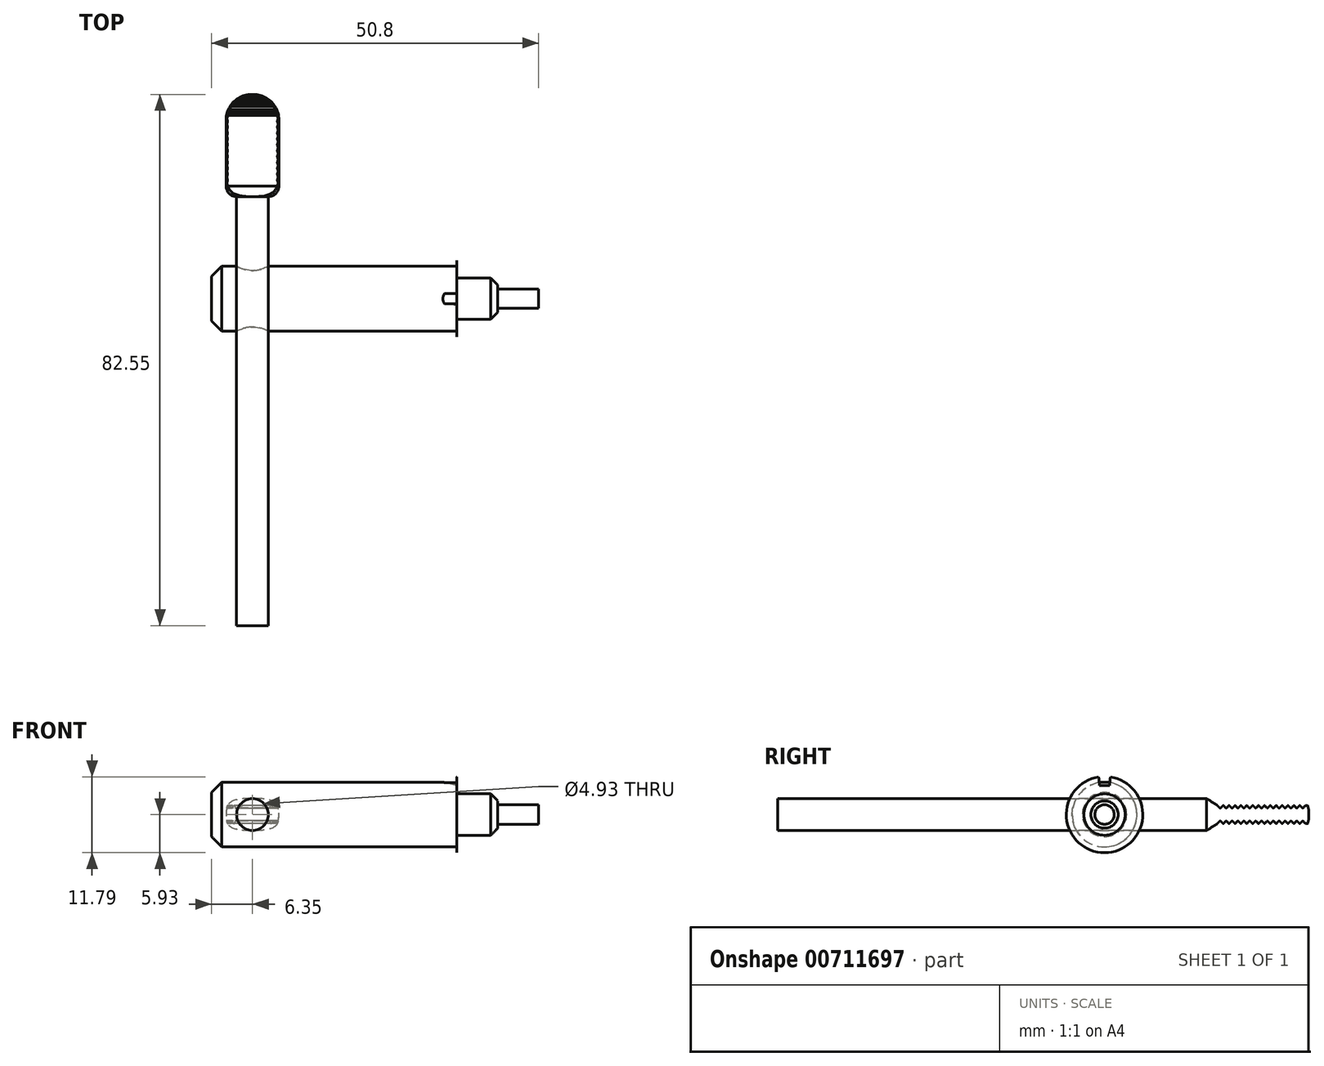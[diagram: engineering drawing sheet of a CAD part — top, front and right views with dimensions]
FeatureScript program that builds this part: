
annotation { "Feature Type Name" : "Feature", "Feature Type Description" : "" }
export const myFeature = defineFeature(function(context is Context, id is Id, definition is map)
    precondition{}
    {
        {
            var Q0;
            Q0=qCreatedBy(makeId("Right.planeOp"),FACE);
            var sketch = newSketch(context, id + "F0", { "sketchPlane" : qUnion([Q0])});
            skCircle(sketch, "E0", {"center": v(0, 0) * mm, "radius": 5.03 * mm});
            skSolve(sketch);
        }
        {
            var Q0;
            Q0 = qSketchRegion(id + "F0", true);
            extrude(context, id + "F1", {"entities" : qUnion([Q0]), "depth" : 38.1 * mm, "offsetDistance" : 25.4 * mm});
        }
        {
            var Q0;
            Q0=makeQuery(id+"F1.opExtrude","CAP_FACE",FACE,{"disambiguationData":[OSD([sQuery(id+"F0.wireOp",EDGE,"E0")])],"isStart":false});
            var sketch = newSketch(context, id + "F2", { "sketchPlane" : qUnion([Q0])});
            skCircle(sketch, "E1", {"center": v(0, 0) * mm, "radius": 7.14 * mm});
            skSolve(sketch);
        }
        {
            var Q0;
            Q0 = qSketchRegion(id + "F2", true);
            extrude(context, id + "F3", {"entities" : qUnion([Q0]), "operationType" : NewBodyOperationType.ADD, "oppositeDirection" : true, "depth" : 5 / 406.4 * mm, "offsetDistance" : 25.4 * mm, "hasDraft" : true, "draftAngle" : 22 * degree});
        }
        {
            var Q0;
            Q0=makeQuery(id+"F3.boolean.opBoolean","MERGE",FACE,{"derivedFrom":[makeQuery(id+"F1.opExtrude","CAP_FACE",FACE,{"disambiguationData":[OSD([sQuery(id+"F0.wireOp",EDGE,"E0")])],"isStart":false}),makeQuery(id+"F3.opExtrude","CAP_FACE",FACE,{"disambiguationData":[OSD([sQuery(id+"F2.wireOp",EDGE,"E1")])],"isStart":true})]});
            var sketch = newSketch(context, id + "F4", { "sketchPlane" : qUnion([Q0])});
            skCircle(sketch, "E2", {"center": v(0, 0) * mm, "radius": 3.22 * mm});
            skSolve(sketch);
        }
        {
            var Q0;
            Q0 = qSketchRegion(id + "F4", true);
            extrude(context, id + "F5", {"entities" : qUnion([Q0]), "operationType" : NewBodyOperationType.ADD, "depth" : 6.35 * mm, "offsetDistance" : 25.4 * mm});
        }
        {
            var Q0;
            Q0=makeQuery(id+"F5.opExtrude","CAP_FACE",FACE,{"disambiguationData":[OSD([sQuery(id+"F4.wireOp",EDGE,"E2")])],"isStart":false});
            var sketch = newSketch(context, id + "F6", { "sketchPlane" : qUnion([Q0])});
            skCircle(sketch, "E3", {"center": v(0, 0) * mm, "radius": 1.51 * mm});
            skSolve(sketch);
        }
        {
            var Q0;
            Q0 = qSketchRegion(id + "F6", true);
            extrude(context, id + "F7", {"entities" : qUnion([Q0]), "operationType" : NewBodyOperationType.ADD, "depth" : 6.35 * mm, "offsetDistance" : 25.4 * mm});
        }
        {
            var Q0;
            Q0=makeQuery(id+"F5.opExtrude","CAP_EDGE",EDGE,{"disambiguationData":[OSD([sQuery(id+"F4.wireOp",EDGE,"E2")])],"isStart":false});
            chamfer(context, id + "F8", {"entities" : qUnion([Q0]), "chamferType" : ChamferType.OFFSET_ANGLE, "width" : 1.1 * mm, "oppositeDirection" : false, "angle" : 45 * degree, "tangentPropagation" : true});
        }
        {
            var Q0;
            Q0=makeQuery(id+"F1.opExtrude","CAP_EDGE",EDGE,{"disambiguationData":[OSD([sQuery(id+"F0.wireOp",EDGE,"E0")])],"isStart":true});
            chamfer(context, id + "F9", {"entities" : qUnion([Q0]), "chamferType" : ChamferType.OFFSET_ANGLE, "width" : 1.59 * mm, "oppositeDirection" : false, "angle" : 45 * degree, "tangentPropagation" : true});
        }
        {
            var Q0;
            Q0=makeQuery(id+"F3.opExtrude","CAP_EDGE",EDGE,{"disambiguationData":[OSD([sQuery(id+"F2.wireOp",EDGE,"E1")])],"isStart":false});
            chamfer(context, id + "F10", {"entities" : qUnion([Q0]), "chamferType" : ChamferType.OFFSET_ANGLE, "width" : 1.59 * mm, "oppositeDirection" : false, "angle" : 45 * degree, "tangentPropagation" : true});
        }
        {
            var Q0;
            Q0=qCreatedBy(makeId("Front.planeOp"),FACE);
            var sketch = newSketch(context, id + "F11", { "sketchPlane" : qUnion([Q0])});
            skLineSegment(sketch, "E4", {"start": v(57.18, 0) * mm, "end": v(30.16, 6.4) * mm});
            skLineSegment(sketch, "E5", {"start": v(30.16, 0) * mm, "end": v(0, 0) * mm});
            skLineSegment(sketch, "E6", {"start": v(30.16, 6.4) * mm, "end": v(30.16, 11.7) * mm});
            skLineSegment(sketch, "E7", {"start": v(30.16, 11.7) * mm, "end": v(57.18, 0) * mm});
            skSolve(sketch);
        }
        {
            var Q0;
            Q0 = qSketchRegion(id + "F11", true);
            extrude(context, id + "F12", {"entities" : qUnion([Q0]), "operationType" : NewBodyOperationType.REMOVE, "depth" : 0.8 * mm, "offsetDistance" : 25.4 * mm, "hasSecondDirection" : true, "secondDirectionOppositeDirection" : true, "secondDirectionDepth" : 0.8 * mm});
        }
        {
            var Q0;
            {var subQ3=sQuery(id+"F11.wireOp",EDGE,"E4");Q0=makeQuery(id+"F12.boolean.opBoolean","COPY",FACE,{"disambiguationData":[TD([makeQuery(id+"F1.opExtrude","CAP_FACE",FACE,{"disambiguationData":[OSD([sQuery(id+"F0.wireOp",EDGE,"E0")])],"isStart":false})])],"derivedFrom":makeQuery(id+"F12.opExtrude","SWEPT_FACE",FACE,{"disambiguationData":[OSD([subQ3])]})});}
            var sketch = newSketch(context, id + "F13", { "sketchPlane" : qUnion([Q0])});
            skLineSegment(sketch, "E8.bottom", {"start": v(34.32, -0.8) * mm, "end": v(31.78, -0.8) * mm});
            skLineSegment(sketch, "E8.top", {"start": v(34.32, 0.8) * mm, "end": v(31.78, 0.8) * mm});
            skLineSegment(sketch, "E8.left", {"start": v(34.32, -0.8) * mm, "end": v(34.32, 0.8) * mm});
            skLineSegment(sketch, "E8.right", {"start": v(31.78, -0.8) * mm, "end": v(31.78, 0.8) * mm});
            skSolve(sketch);
        }
        {
            var Q0;
            Q0 = qSketchRegion(id + "F13", true);
            extrude(context, id + "F14", {"entities" : qUnion([Q0]), "operationType" : NewBodyOperationType.ADD, "depth" : 12.7 * mm, "offsetDistance" : 25.4 * mm});
        }
        {
            var Q0;
            Q0=makeQuery(id+"F14.opExtrude","SWEPT_FACE",FACE,{"disambiguationData":[OSD([sQuery(id+"F13.wireOp",EDGE,"E8.left")])]});
            var sketch = newSketch(context, id + "F15", { "sketchPlane" : qUnion([Q0])});
            skFitSpline(sketch, "E9", {"points": [v(0.8, 13.16) * mm, v(0.85, 13.93) * mm, v(1.13, 15.04) * mm, v(2.24, 16.6) * mm], "startDerivative": vector(0.1, 2.28) * mm, "endDerivative": vector(1.27, 1.84) * mm});
            skLineSegment(sketch, "E10", {"start": v(-0.8, 13.16) * mm, "end": v(0.8, 13.16) * mm});
            skFitSpline(sketch, "E11.MirrorCS", {"points": [v(-0.8, 13.16) * mm, v(-0.85, 13.93) * mm, v(-1.13, 15.04) * mm, v(-2.24, 16.6) * mm], "startDerivative": vector(-0.1, 2.28) * mm, "endDerivative": vector(-1.27, 1.84) * mm});
            skArc(sketch, "E12", {"start": v(2.24, 16.6) * mm, "mid": v(0, 17.44) * mm, "end": v(-2.24, 16.6) * mm});
            skSolve(sketch);
        }
        {
            var Q0;
            Q0 = qSketchRegion(id + "F15", true);
            extrude(context, id + "F16", {"entities" : qUnion([Q0]), "operationType" : NewBodyOperationType.REMOVE, "depth" : 25.4 * mm, "offsetDistance" : 25.4 * mm, "hasSecondDirection" : true, "secondDirectionOppositeDirection" : true, "secondDirectionDepth" : 25.4 * mm});
        }
        {
            var Q0;
            Q0=makeQuery(id+"F14.opExtrude","SWEPT_FACE",FACE,{"disambiguationData":[OSD([sQuery(id+"F13.wireOp",EDGE,"E8.left")])]});
            var sketch = newSketch(context, id + "F17", { "sketchPlane" : qUnion([Q0])});
            skLineSegment(sketch, "E13.bottom", {"start": v(-0.8, 25.86) * mm, "end": v(0.8, 25.86) * mm});
            skLineSegment(sketch, "E13.top", {"start": v(-0.8, 17.34) * mm, "end": v(0.8, 17.34) * mm});
            skLineSegment(sketch, "E13.left", {"start": v(-0.8, 25.86) * mm, "end": v(-0.8, 17.34) * mm});
            skLineSegment(sketch, "E13.right", {"start": v(0.8, 25.86) * mm, "end": v(0.8, 17.34) * mm});
            skSolve(sketch);
        }
        {
            var Q0;
            Q0 = qSketchRegion(id + "F17", true);
            extrude(context, id + "F18", {"entities" : qUnion([Q0]), "operationType" : NewBodyOperationType.REMOVE, "oppositeDirection" : true, "depth" : 25.4 * mm, "offsetDistance" : 25.4 * mm});
        }
        {
            var Q0;
            Q0=qCreatedBy(makeId("Front.planeOp"),FACE);
            var sketch = newSketch(context, id + "F19", { "sketchPlane" : qUnion([Q0])});
            skCircle(sketch, "E14", {"center": v(6.35, 0) * mm, "radius": 2.46 * mm});
            skSolve(sketch);
        }
        {
            var Q0;
            Q0 = qSketchRegion(id + "F19", true);
            extrude(context, id + "F20", {"entities" : qUnion([Q0]), "operationType" : NewBodyOperationType.REMOVE, "oppositeDirection" : true, "depth" : 25.4 * mm, "offsetDistance" : 25.4 * mm, "hasSecondDirection" : true, "secondDirectionOppositeDirection" : false, "secondDirectionDepth" : 25.4 * mm});
        }
        {
            var Q0;
            Q0=qCreatedBy(makeId("Front.planeOp"),FACE);
            var sketch = newSketch(context, id + "F21", { "sketchPlane" : qUnion([Q0])});
            skCircle(sketch, "E15", {"center": v(6.35, 0) * mm, "radius": 2.46 * mm});
            skSolve(sketch);
        }
        {
            var Q0;
            Q0 = qSketchRegion(id + "F21", true);
            extrude(context, id + "F22", {"entities" : qUnion([Q0]), "depth" : 50.8 * mm, "offsetDistance" : 25.4 * mm, "hasSecondDirection" : true, "secondDirectionOppositeDirection" : true, "secondDirectionDepth" : 31.75 * mm});
        }
        {
            var Q0;
            Q0=makeQuery(id+"F22.opExtrude","CAP_FACE",FACE,{"disambiguationData":[OSD([sQuery(id+"F21.wireOp",EDGE,"E15")])],"isStart":true});
            var sketch = newSketch(context, id + "F23", { "sketchPlane" : qUnion([Q0])});
            skCircle(sketch, "E16", {"center": v(-6.35, 0) * mm, "radius": 4.1 * mm});
            skSolve(sketch);
        }
        {
            var Q0;
            Q0 = qSketchRegion(id + "F23", true);
            extrude(context, id + "F24", {"entities" : qUnion([Q0]), "operationType" : NewBodyOperationType.ADD, "oppositeDirection" : true, "depth" : 15.88 * mm, "offsetDistance" : 25.4 * mm});
        }
        {
            var Q0;
            Q0=qCreatedBy(makeId("Right.planeOp"),FACE);
            var sketch = newSketch(context, id + "F25", { "sketchPlane" : qUnion([Q0])});
            skLineSegment(sketch, "E17.bottom", {"start": v(31.75, 1.42) * mm, "end": v(31.24, 1.42) * mm});
            skLineSegment(sketch, "E17.top", {"start": v(31.75, 6.1) * mm, "end": v(15.88, 6.1) * mm});
            skLineSegment(sketch, "E17.left", {"start": v(31.75, 1.42) * mm, "end": v(31.75, 6.1) * mm});
            skLineSegment(sketch, "E17.right", {"start": v(15.88, 2.48) * mm, "end": v(15.88, 6.1) * mm});
            skLineSegment(sketch, "E18", {"start": v(15.88, 2.48) * mm, "end": v(17.52, 1.42) * mm});
            skLineSegment(sketch, "E19", {"start": v(17.52, 1.42) * mm, "end": v(17.89, 1.06) * mm});
            skLineSegment(sketch, "E20", {"start": v(18.07, 1.06) * mm, "end": v(18.38, 1.37) * mm});
            skLineSegment(sketch, "E21.1.0.0", {"start": v(18.49, 1.37) * mm, "end": v(18.84, 1.02) * mm});
            skLineSegment(sketch, "E21.1.0.1", {"start": v(18.95, 1.02) * mm, "end": v(19.3, 1.37) * mm});
            skLineSegment(sketch, "E21.2.0.0", {"start": v(19.4, 1.37) * mm, "end": v(19.75, 1.02) * mm});
            skLineSegment(sketch, "E21.2.0.1", {"start": v(19.86, 1.02) * mm, "end": v(20.21, 1.37) * mm});
            skLineSegment(sketch, "E21.3.0.0", {"start": v(20.32, 1.37) * mm, "end": v(20.67, 1.02) * mm});
            skLineSegment(sketch, "E21.3.0.1", {"start": v(20.78, 1.02) * mm, "end": v(21.13, 1.37) * mm});
            skLineSegment(sketch, "E21.4.0.0", {"start": v(21.23, 1.37) * mm, "end": v(21.58, 1.02) * mm});
            skLineSegment(sketch, "E21.4.0.1", {"start": v(21.7, 1.02) * mm, "end": v(22.04, 1.37) * mm});
            skLineSegment(sketch, "E21.5.0.0", {"start": v(22.15, 1.37) * mm, "end": v(22.5, 1.02) * mm});
            skLineSegment(sketch, "E21.5.0.1", {"start": v(22.6, 1.02) * mm, "end": v(22.95, 1.37) * mm});
            skLineSegment(sketch, "E21.6.0.0", {"start": v(23.06, 1.37) * mm, "end": v(23.41, 1.02) * mm});
            skLineSegment(sketch, "E21.6.0.1", {"start": v(23.52, 1.02) * mm, "end": v(23.87, 1.37) * mm});
            skLineSegment(sketch, "E21.7.0.0", {"start": v(23.98, 1.37) * mm, "end": v(24.33, 1.02) * mm});
            skLineSegment(sketch, "E21.7.0.1", {"start": v(24.43, 1.02) * mm, "end": v(24.78, 1.37) * mm});
            skLineSegment(sketch, "E21.8.0.0", {"start": v(24.9, 1.37) * mm, "end": v(25.24, 1.02) * mm});
            skLineSegment(sketch, "E21.8.0.1", {"start": v(25.35, 1.02) * mm, "end": v(25.7, 1.37) * mm});
            skLineSegment(sketch, "E21.9.0.0", {"start": v(25.8, 1.37) * mm, "end": v(26.15, 1.02) * mm});
            skLineSegment(sketch, "E21.9.0.1", {"start": v(26.26, 1.02) * mm, "end": v(26.61, 1.37) * mm});
            skLineSegment(sketch, "E21.10.0.0", {"start": v(26.72, 1.37) * mm, "end": v(27.07, 1.02) * mm});
            skLineSegment(sketch, "E21.10.0.1", {"start": v(27.18, 1.02) * mm, "end": v(27.53, 1.37) * mm});
            skLineSegment(sketch, "E21.11.0.0", {"start": v(27.63, 1.37) * mm, "end": v(27.98, 1.02) * mm});
            skLineSegment(sketch, "E21.11.0.1", {"start": v(28.1, 1.02) * mm, "end": v(28.5, 1.42) * mm});
            skLineSegment(sketch, "E21.12.0.0", {"start": v(28.5, 1.42) * mm, "end": v(28.95, 0.97) * mm});
            skLineSegment(sketch, "E21.12.0.1", {"start": v(28.95, 0.97) * mm, "end": v(29.4, 1.42) * mm});
            skLineSegment(sketch, "E21.13.0.0", {"start": v(29.4, 1.42) * mm, "end": v(29.87, 0.97) * mm});
            skLineSegment(sketch, "E21.13.0.1", {"start": v(29.87, 0.97) * mm, "end": v(30.32, 1.42) * mm});
            skLineSegment(sketch, "E21.direction1", {"start": v(17.98, 0.97) * mm, "end": v(18.9, 0.97) * mm, "construction": true});
            skLineSegment(sketch, "E22.0.14.0", {"start": v(30.32, 1.42) * mm, "end": v(30.78, 0.97) * mm});
            skLineSegment(sketch, "E22.3.14.0", {"start": v(30.78, 0.97) * mm, "end": v(31.24, 1.42) * mm});
            skPoint(sketch, "E23.visualSharp", {"position": v(17.98, 0.97) * mm});
            skArc(sketch, "E23.filletArc", {"start": v(17.89, 1.06) * mm, "mid": v(17.98, 1.02) * mm, "end": v(18.07, 1.06) * mm});
            skPoint(sketch, "E24.visualSharp", {"position": v(18.44, 1.42) * mm});
            skArc(sketch, "E24.filletArc", {"start": v(18.49, 1.37) * mm, "mid": v(18.44, 1.4) * mm, "end": v(18.38, 1.37) * mm});
            skPoint(sketch, "E25.visualSharp", {"position": v(18.9, 0.97) * mm});
            skArc(sketch, "E25.filletArc", {"start": v(18.84, 1.02) * mm, "mid": v(18.9, 1) * mm, "end": v(18.95, 1.02) * mm});
            skPoint(sketch, "E26.visualSharp", {"position": v(19.35, 1.42) * mm});
            skArc(sketch, "E26.filletArc", {"start": v(19.4, 1.37) * mm, "mid": v(19.35, 1.4) * mm, "end": v(19.3, 1.37) * mm});
            skPoint(sketch, "E27.visualSharp", {"position": v(19.8, 0.97) * mm});
            skArc(sketch, "E27.filletArc", {"start": v(19.75, 1.02) * mm, "mid": v(19.8, 1) * mm, "end": v(19.86, 1.02) * mm});
            skPoint(sketch, "E28.visualSharp", {"position": v(20.26, 1.42) * mm});
            skArc(sketch, "E28.filletArc", {"start": v(20.32, 1.37) * mm, "mid": v(20.26, 1.4) * mm, "end": v(20.21, 1.37) * mm});
            skPoint(sketch, "E29.visualSharp", {"position": v(20.72, 0.97) * mm});
            skArc(sketch, "E29.filletArc", {"start": v(20.67, 1.02) * mm, "mid": v(20.72, 1) * mm, "end": v(20.78, 1.02) * mm});
            skPoint(sketch, "E30.visualSharp", {"position": v(21.18, 1.42) * mm});
            skArc(sketch, "E30.filletArc", {"start": v(21.23, 1.37) * mm, "mid": v(21.18, 1.4) * mm, "end": v(21.13, 1.37) * mm});
            skPoint(sketch, "E31.visualSharp", {"position": v(21.64, 0.97) * mm});
            skArc(sketch, "E31.filletArc", {"start": v(21.58, 1.02) * mm, "mid": v(21.64, 1) * mm, "end": v(21.7, 1.02) * mm});
            skPoint(sketch, "E32.visualSharp", {"position": v(22.1, 1.42) * mm});
            skArc(sketch, "E32.filletArc", {"start": v(22.15, 1.37) * mm, "mid": v(22.1, 1.4) * mm, "end": v(22.04, 1.37) * mm});
            skPoint(sketch, "E33.visualSharp", {"position": v(22.55, 0.97) * mm});
            skArc(sketch, "E33.filletArc", {"start": v(22.5, 1.02) * mm, "mid": v(22.55, 1) * mm, "end": v(22.6, 1.02) * mm});
            skPoint(sketch, "E34.visualSharp", {"position": v(23, 1.42) * mm});
            skArc(sketch, "E34.filletArc", {"start": v(23.06, 1.37) * mm, "mid": v(23, 1.4) * mm, "end": v(22.95, 1.37) * mm});
            skPoint(sketch, "E35.visualSharp", {"position": v(23.92, 1.42) * mm});
            skArc(sketch, "E35.filletArc", {"start": v(23.98, 1.37) * mm, "mid": v(23.92, 1.4) * mm, "end": v(23.87, 1.37) * mm});
            skPoint(sketch, "E36.visualSharp", {"position": v(23.47, 0.97) * mm});
            skArc(sketch, "E36.filletArc", {"start": v(23.41, 1.02) * mm, "mid": v(23.47, 1) * mm, "end": v(23.52, 1.02) * mm});
            skPoint(sketch, "E37.visualSharp", {"position": v(24.38, 0.97) * mm});
            skArc(sketch, "E37.filletArc", {"start": v(24.33, 1.02) * mm, "mid": v(24.38, 1) * mm, "end": v(24.43, 1.02) * mm});
            skPoint(sketch, "E38.visualSharp", {"position": v(24.84, 1.42) * mm});
            skArc(sketch, "E38.filletArc", {"start": v(24.9, 1.37) * mm, "mid": v(24.84, 1.4) * mm, "end": v(24.78, 1.37) * mm});
            skPoint(sketch, "E39.visualSharp", {"position": v(25.75, 1.42) * mm});
            skArc(sketch, "E39.filletArc", {"start": v(25.8, 1.37) * mm, "mid": v(25.75, 1.4) * mm, "end": v(25.7, 1.37) * mm});
            skPoint(sketch, "E40.visualSharp", {"position": v(25.3, 0.97) * mm});
            skArc(sketch, "E40.filletArc", {"start": v(25.24, 1.02) * mm, "mid": v(25.3, 1) * mm, "end": v(25.35, 1.02) * mm});
            skPoint(sketch, "E41.visualSharp", {"position": v(26.2, 0.97) * mm});
            skArc(sketch, "E41.filletArc", {"start": v(26.15, 1.02) * mm, "mid": v(26.2, 1) * mm, "end": v(26.26, 1.02) * mm});
            skPoint(sketch, "E42.visualSharp", {"position": v(26.67, 1.42) * mm});
            skArc(sketch, "E42.filletArc", {"start": v(26.72, 1.37) * mm, "mid": v(26.67, 1.4) * mm, "end": v(26.61, 1.37) * mm});
            skPoint(sketch, "E43.visualSharp", {"position": v(27.58, 1.42) * mm});
            skArc(sketch, "E43.filletArc", {"start": v(27.63, 1.37) * mm, "mid": v(27.58, 1.4) * mm, "end": v(27.53, 1.37) * mm});
            skPoint(sketch, "E44.visualSharp", {"position": v(27.12, 0.97) * mm});
            skArc(sketch, "E44.filletArc", {"start": v(27.07, 1.02) * mm, "mid": v(27.12, 1) * mm, "end": v(27.18, 1.02) * mm});
            skPoint(sketch, "E45.visualSharp", {"position": v(28.04, 0.97) * mm});
            skArc(sketch, "E45.filletArc", {"start": v(27.98, 1.02) * mm, "mid": v(28.04, 1) * mm, "end": v(28.1, 1.02) * mm});
            skLineSegment(sketch, "E46.MirrorCS", {"start": v(19.4, -1.37) * mm, "end": v(19.75, -1.02) * mm});
            skArc(sketch, "E47.MirrorCS", {"start": v(22.15, -1.37) * mm, "mid": v(22.1, -1.4) * mm, "end": v(22.04, -1.37) * mm});
            skLineSegment(sketch, "E48.MirrorCS", {"start": v(18.95, -1.02) * mm, "end": v(19.3, -1.37) * mm});
            skLineSegment(sketch, "E49.MirrorCS", {"start": v(20.32, -1.37) * mm, "end": v(20.67, -1.02) * mm});
            skLineSegment(sketch, "E50.MirrorCS", {"start": v(19.86, -1.02) * mm, "end": v(20.21, -1.37) * mm});
            skLineSegment(sketch, "E51.MirrorCS", {"start": v(22.15, -1.37) * mm, "end": v(22.5, -1.02) * mm});
            skLineSegment(sketch, "E52.MirrorCS", {"start": v(21.7, -1.02) * mm, "end": v(22.04, -1.37) * mm});
            skLineSegment(sketch, "E53.MirrorCS", {"start": v(22.6, -1.02) * mm, "end": v(22.95, -1.37) * mm});
            skArc(sketch, "E54.MirrorCS", {"start": v(25.8, -1.37) * mm, "mid": v(25.75, -1.4) * mm, "end": v(25.7, -1.37) * mm});
            skLineSegment(sketch, "E55.MirrorCS", {"start": v(20.78, -1.02) * mm, "end": v(21.13, -1.37) * mm});
            skArc(sketch, "E56.MirrorCS", {"start": v(27.98, -1.02) * mm, "mid": v(28.04, -1) * mm, "end": v(28.1, -1.02) * mm});
            skLineSegment(sketch, "E57.MirrorCS", {"start": v(21.23, -1.37) * mm, "end": v(21.58, -1.02) * mm});
            skArc(sketch, "E58.MirrorCS", {"start": v(19.4, -1.37) * mm, "mid": v(19.35, -1.4) * mm, "end": v(19.3, -1.37) * mm});
            skArc(sketch, "E59.MirrorCS", {"start": v(20.67, -1.02) * mm, "mid": v(20.72, -1) * mm, "end": v(20.78, -1.02) * mm});
            skLineSegment(sketch, "E60.MirrorCS", {"start": v(27.18, -1.02) * mm, "end": v(27.53, -1.37) * mm});
            skArc(sketch, "E61.MirrorCS", {"start": v(23.06, -1.37) * mm, "mid": v(23, -1.4) * mm, "end": v(22.95, -1.37) * mm});
            skArc(sketch, "E62.MirrorCS", {"start": v(21.58, -1.02) * mm, "mid": v(21.64, -1) * mm, "end": v(21.7, -1.02) * mm});
            skLineSegment(sketch, "E63.MirrorCS", {"start": v(25.35, -1.02) * mm, "end": v(25.7, -1.37) * mm});
            skArc(sketch, "E64.MirrorCS", {"start": v(22.5, -1.02) * mm, "mid": v(22.55, -1) * mm, "end": v(22.6, -1.02) * mm});
            skLineSegment(sketch, "E65.MirrorCS", {"start": v(26.26, -1.02) * mm, "end": v(26.61, -1.37) * mm});
            skArc(sketch, "E66.MirrorCS", {"start": v(19.75, -1.02) * mm, "mid": v(19.8, -1) * mm, "end": v(19.86, -1.02) * mm});
            skArc(sketch, "E67.MirrorCS", {"start": v(18.84, -1.02) * mm, "mid": v(18.9, -1) * mm, "end": v(18.95, -1.02) * mm});
            skArc(sketch, "E68.MirrorCS", {"start": v(20.32, -1.37) * mm, "mid": v(20.26, -1.4) * mm, "end": v(20.21, -1.37) * mm});
            skArc(sketch, "E69.MirrorCS", {"start": v(21.23, -1.37) * mm, "mid": v(21.18, -1.4) * mm, "end": v(21.13, -1.37) * mm});
            skArc(sketch, "E70.MirrorCS", {"start": v(26.72, -1.37) * mm, "mid": v(26.67, -1.4) * mm, "end": v(26.61, -1.37) * mm});
            skLineSegment(sketch, "E71.MirrorCS", {"start": v(25.8, -1.37) * mm, "end": v(26.15, -1.02) * mm});
            skLineSegment(sketch, "E72.MirrorCS", {"start": v(28.1, -1.02) * mm, "end": v(28.5, -1.42) * mm});
            skLineSegment(sketch, "E73.MirrorCS", {"start": v(28.5, -1.42) * mm, "end": v(28.95, -0.97) * mm});
            skLineSegment(sketch, "E74.MirrorCS", {"start": v(26.72, -1.37) * mm, "end": v(27.07, -1.02) * mm});
            skArc(sketch, "E75.MirrorCS", {"start": v(27.63, -1.37) * mm, "mid": v(27.58, -1.4) * mm, "end": v(27.53, -1.37) * mm});
            skLineSegment(sketch, "E76.MirrorCS", {"start": v(27.63, -1.37) * mm, "end": v(27.98, -1.02) * mm});
            skArc(sketch, "E77.MirrorCS", {"start": v(26.15, -1.02) * mm, "mid": v(26.2, -1) * mm, "end": v(26.26, -1.02) * mm});
            skArc(sketch, "E78.MirrorCS", {"start": v(27.07, -1.02) * mm, "mid": v(27.12, -1) * mm, "end": v(27.18, -1.02) * mm});
            skArc(sketch, "E79.MirrorCS", {"start": v(25.24, -1.02) * mm, "mid": v(25.3, -1) * mm, "end": v(25.35, -1.02) * mm});
            skLineSegment(sketch, "E80.MirrorCS", {"start": v(18.49, -1.37) * mm, "end": v(18.84, -1.02) * mm});
            skLineSegment(sketch, "E81.MirrorCS", {"start": v(23.06, -1.37) * mm, "end": v(23.41, -1.02) * mm});
            skArc(sketch, "E82.MirrorCS", {"start": v(17.89, -1.06) * mm, "mid": v(17.98, -1.02) * mm, "end": v(18.07, -1.06) * mm});
            skLineSegment(sketch, "E83.MirrorCS", {"start": v(23.52, -1.02) * mm, "end": v(23.87, -1.37) * mm});
            skLineSegment(sketch, "E84.MirrorCS", {"start": v(23.98, -1.37) * mm, "end": v(24.33, -1.02) * mm});
            skArc(sketch, "E85.MirrorCS", {"start": v(23.98, -1.37) * mm, "mid": v(23.92, -1.4) * mm, "end": v(23.87, -1.37) * mm});
            skLineSegment(sketch, "E86.MirrorCS", {"start": v(18.07, -1.06) * mm, "end": v(18.38, -1.37) * mm});
            skLineSegment(sketch, "E87.MirrorCS", {"start": v(17.98, -0.97) * mm, "end": v(18.9, -0.97) * mm, "construction": true});
            skArc(sketch, "E88.MirrorCS", {"start": v(23.41, -1.02) * mm, "mid": v(23.47, -1) * mm, "end": v(23.52, -1.02) * mm});
            skArc(sketch, "E89.MirrorCS", {"start": v(18.49, -1.37) * mm, "mid": v(18.44, -1.4) * mm, "end": v(18.38, -1.37) * mm});
            skLineSegment(sketch, "E90.MirrorCS", {"start": v(17.52, -1.42) * mm, "end": v(17.89, -1.06) * mm});
            skArc(sketch, "E91.MirrorCS", {"start": v(24.9, -1.37) * mm, "mid": v(24.84, -1.4) * mm, "end": v(24.78, -1.37) * mm});
            skLineSegment(sketch, "E92.MirrorCS", {"start": v(24.43, -1.02) * mm, "end": v(24.78, -1.37) * mm});
            skArc(sketch, "E93.MirrorCS", {"start": v(24.33, -1.02) * mm, "mid": v(24.38, -1) * mm, "end": v(24.43, -1.02) * mm});
            skLineSegment(sketch, "E94.MirrorCS", {"start": v(28.95, -0.97) * mm, "end": v(29.4, -1.42) * mm});
            skLineSegment(sketch, "E95.MirrorCS", {"start": v(29.4, -1.42) * mm, "end": v(29.87, -0.97) * mm});
            skLineSegment(sketch, "E96.MirrorCS", {"start": v(24.9, -1.37) * mm, "end": v(25.24, -1.02) * mm});
            skLineSegment(sketch, "E97.MirrorCS", {"start": v(30.32, -1.42) * mm, "end": v(30.78, -0.97) * mm});
            skLineSegment(sketch, "E98.MirrorCS", {"start": v(31.75, -1.42) * mm, "end": v(31.24, -1.42) * mm});
            skLineSegment(sketch, "E99.MirrorCS", {"start": v(29.87, -0.97) * mm, "end": v(30.32, -1.42) * mm});
            skLineSegment(sketch, "E100.MirrorCS", {"start": v(30.78, -0.97) * mm, "end": v(31.24, -1.42) * mm});
            skLineSegment(sketch, "E101.MirrorCS", {"start": v(15.88, -2.48) * mm, "end": v(17.52, -1.42) * mm});
            skLineSegment(sketch, "E102.MirrorCS", {"start": v(15.88, -2.48) * mm, "end": v(15.88, -6.1) * mm});
            skPoint(sketch, "E103.MirrorP", {"position": v(22.55, -0.97) * mm});
            skPoint(sketch, "E104.MirrorP", {"position": v(22.1, -1.42) * mm});
            skPoint(sketch, "E105.MirrorP", {"position": v(19.8, -0.97) * mm});
            skPoint(sketch, "E106.MirrorP", {"position": v(17.98, -0.97) * mm});
            skPoint(sketch, "E107.MirrorP", {"position": v(27.58, -1.42) * mm});
            skPoint(sketch, "E108.MirrorP", {"position": v(19.35, -1.42) * mm});
            skPoint(sketch, "E109.MirrorP", {"position": v(21.18, -1.42) * mm});
            skPoint(sketch, "E110.MirrorP", {"position": v(20.26, -1.42) * mm});
            skLineSegment(sketch, "E111.MirrorCS", {"start": v(31.75, -6.1) * mm, "end": v(15.88, -6.1) * mm});
            skLineSegment(sketch, "E112.MirrorCS", {"start": v(31.75, -1.42) * mm, "end": v(31.75, -6.1) * mm});
            skPoint(sketch, "E113.MirrorP", {"position": v(24.38, -0.97) * mm});
            skPoint(sketch, "E114.MirrorP", {"position": v(28.04, -0.97) * mm});
            skPoint(sketch, "E115.MirrorP", {"position": v(20.72, -0.97) * mm});
            skPoint(sketch, "E116.MirrorP", {"position": v(26.2, -0.97) * mm});
            skPoint(sketch, "E117.MirrorP", {"position": v(18.9, -0.97) * mm});
            skPoint(sketch, "E118.MirrorP", {"position": v(18.44, -1.42) * mm});
            skPoint(sketch, "E119.MirrorP", {"position": v(23.92, -1.42) * mm});
            skPoint(sketch, "E120.MirrorP", {"position": v(26.67, -1.42) * mm});
            skPoint(sketch, "E121.MirrorP", {"position": v(24.84, -1.42) * mm});
            skPoint(sketch, "E122.MirrorP", {"position": v(27.12, -0.97) * mm});
            skPoint(sketch, "E123.MirrorP", {"position": v(25.75, -1.42) * mm});
            skPoint(sketch, "E124.MirrorP", {"position": v(21.64, -0.97) * mm});
            skPoint(sketch, "E125.MirrorP", {"position": v(25.3, -0.97) * mm});
            skPoint(sketch, "E126.MirrorP", {"position": v(23.47, -0.97) * mm});
            skPoint(sketch, "E127.MirrorP", {"position": v(23, -1.42) * mm});
            skSolve(sketch);
        }
        {
            var Q0;
            Q0=makeQuery(id+"F24.boolean.opBoolean","MERGE",FACE,{"derivedFrom":[makeQuery(id+"F22.opExtrude","CAP_FACE",FACE,{"disambiguationData":[OSD([sQuery(id+"F21.wireOp",EDGE,"E15")])],"isStart":true}),makeQuery(id+"F24.opExtrude","CAP_FACE",FACE,{"disambiguationData":[OSD([sQuery(id+"F23.wireOp",EDGE,"E16")])],"isStart":true})]});
            fillet(context, id + "F26", {"entities" : qUnion([Q0]), "radius" : 3.97 * mm, "allowEdgeOverflow" : false});
        }
        {
            var Q0;
            Q0=makeQuery(id+"F24.opExtrude","CAP_EDGE",EDGE,{"disambiguationData":[OSD([sQuery(id+"F23.wireOp",EDGE,"E16")])],"isStart":false});
            fillet(context, id + "F27", {"entities" : qUnion([Q0]), "radius" : 1.63 * mm, "tangentPropagation" : true, "allowEdgeOverflow" : false});
        }
        {
            var Q0;
            Q0 = qSketchRegion(id + "F25", true);
            extrude(context, id + "F28", {"entities" : qUnion([Q0]), "operationType" : NewBodyOperationType.REMOVE, "depth" : 152.4 * mm, "offsetDistance" : 25.4 * mm});
        }
    });
